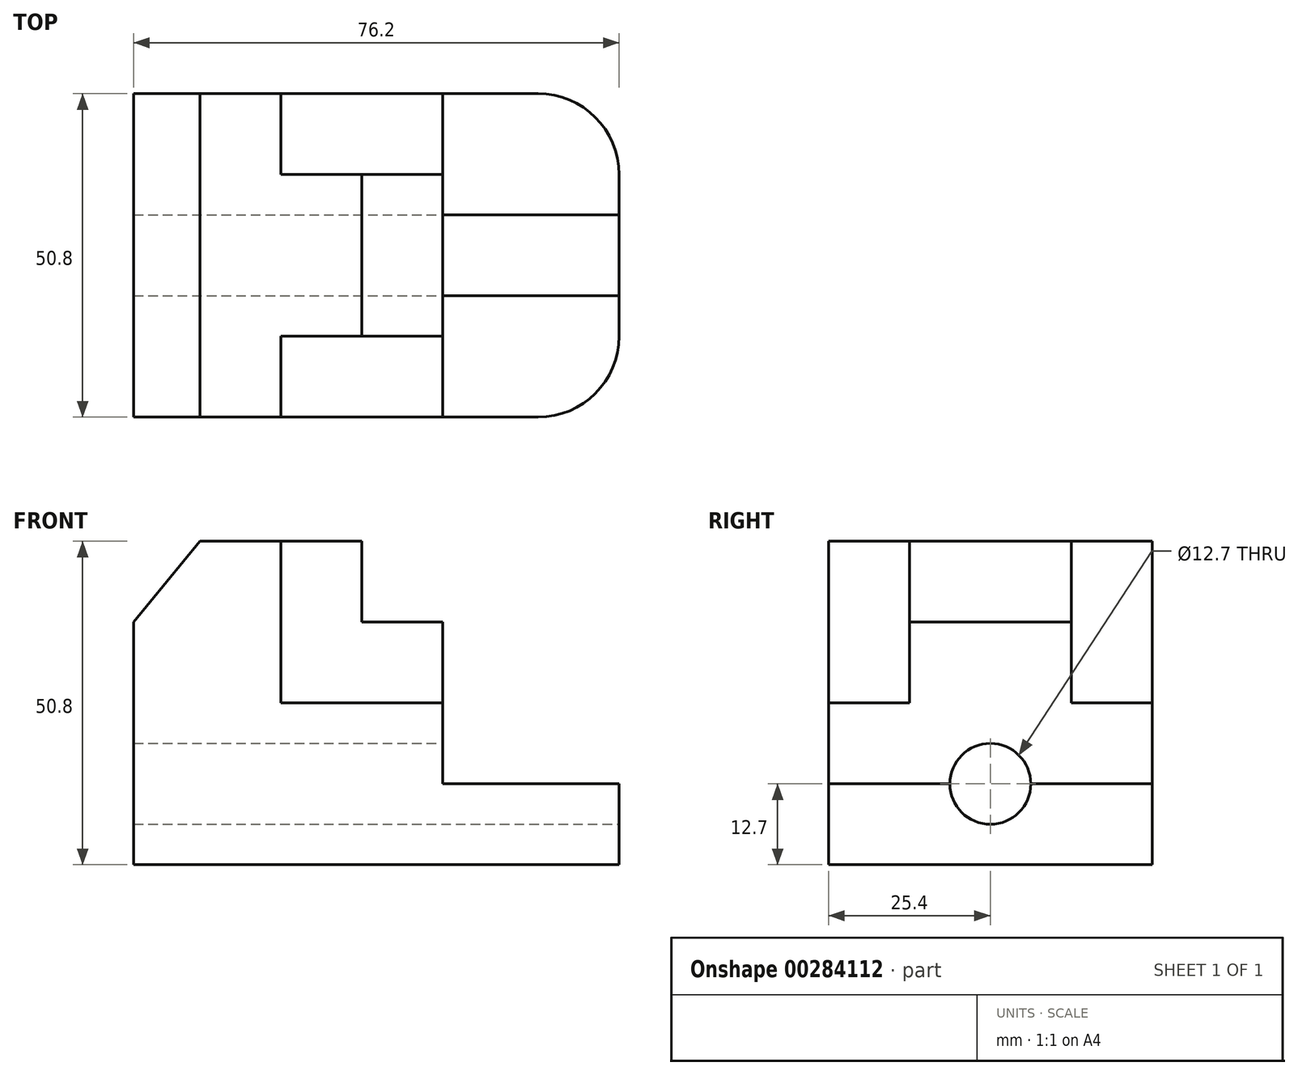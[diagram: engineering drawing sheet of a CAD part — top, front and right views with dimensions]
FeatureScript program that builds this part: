
annotation { "Feature Type Name" : "Feature", "Feature Type Description" : "" }
export const myFeature = defineFeature(function(context is Context, id is Id, definition is map)
    precondition{}
    {
        {
            var Q0;
            Q0=qCreatedBy(makeId("Front.planeOp"),FACE);
            var sketch = newSketch(context, id + "F0", { "sketchPlane" : qUnion([Q0])});
            skLineSegment(sketch, "E0", {"start": v(0, 0) * mm, "end": v(0, 38.1) * mm});
            skLineSegment(sketch, "E1", {"start": v(0, 38.1) * mm, "end": v(10.4, 50.8) * mm});
            skLineSegment(sketch, "E2", {"start": v(10.4, 50.8) * mm, "end": v(35.8, 50.8) * mm});
            skLineSegment(sketch, "E3", {"start": v(35.8, 50.8) * mm, "end": v(35.8, 38.1) * mm});
            skLineSegment(sketch, "E4", {"start": v(35.8, 38.1) * mm, "end": v(48.5, 38.1) * mm});
            skLineSegment(sketch, "E5", {"start": v(48.5, 38.1) * mm, "end": v(48.5, 12.7) * mm});
            skLineSegment(sketch, "E6", {"start": v(48.5, 12.7) * mm, "end": v(76.2, 12.7) * mm});
            skLineSegment(sketch, "E7", {"start": v(76.2, 12.7) * mm, "end": v(76.2, 0) * mm});
            skLineSegment(sketch, "E8", {"start": v(76.2, 0) * mm, "end": v(0, 0) * mm});
            skSolve(sketch);
        }
        {
            var Q0;
            Q0=makeQuery(id+"F0.imprint","IMPRINT",FACE,{"disambiguationData":[TD([[makeQuery(id+"F0.imprint","IMPRINT",EDGE,{"derivedFrom":sQuery(id+"F0.wireOp",EDGE,"E0")}),-1.0]])]});
            extrude(context, id + "F1", {"entities" : qUnion([Q0]), "depth" : 50.8 * mm});
        }
        {
            var Q0;
            Q0=makeQuery(id+"F1.opExtrude","CAP_FACE",FACE,{"disambiguationData":[OSD([sQuery(id+"F0.wireOp",EDGE,"E0"),sQuery(id+"F0.wireOp",EDGE,"E1"),sQuery(id+"F0.wireOp",EDGE,"E2"),sQuery(id+"F0.wireOp",EDGE,"E3"),sQuery(id+"F0.wireOp",EDGE,"E4"),sQuery(id+"F0.wireOp",EDGE,"E5"),sQuery(id+"F0.wireOp",EDGE,"E6"),sQuery(id+"F0.wireOp",EDGE,"E7"),sQuery(id+"F0.wireOp",EDGE,"E8")])],"isStart":false});
            var sketch = newSketch(context, id + "F2", { "sketchPlane" : qUnion([Q0])});
            skLineSegment(sketch, "E9", {"start": v(23.1, 50.8) * mm, "end": v(23.1, 25.4) * mm});
            skLineSegment(sketch, "E10", {"start": v(23.1, 25.4) * mm, "end": v(48.5, 25.4) * mm});
            skLineSegment(sketch, "E11", {"start": v(48.5, 25.4) * mm, "end": v(48.5, 38.1) * mm});
            skLineSegment(sketch, "E12", {"start": v(48.5, 38.1) * mm, "end": v(35.8, 38.1) * mm});
            skLineSegment(sketch, "E13", {"start": v(35.8, 38.1) * mm, "end": v(35.8, 50.8) * mm});
            skLineSegment(sketch, "E14", {"start": v(35.8, 50.8) * mm, "end": v(23.1, 50.8) * mm});
            skSolve(sketch);
        }
        {
            var Q0;
            Q0 = qSketchRegion(id + "F2", true);
            extrude(context, id + "F3", {"entities" : qUnion([Q0]), "operationType" : NewBodyOperationType.REMOVE, "oppositeDirection" : true, "depth" : 12.7 * mm});
        }
        {
            var Q0;
            Q0=makeQuery(id+"F1.opExtrude","CAP_FACE",FACE,{"disambiguationData":[OSD([sQuery(id+"F0.wireOp",EDGE,"E0"),sQuery(id+"F0.wireOp",EDGE,"E1"),sQuery(id+"F0.wireOp",EDGE,"E2"),sQuery(id+"F0.wireOp",EDGE,"E3"),sQuery(id+"F0.wireOp",EDGE,"E4"),sQuery(id+"F0.wireOp",EDGE,"E5"),sQuery(id+"F0.wireOp",EDGE,"E6"),sQuery(id+"F0.wireOp",EDGE,"E7"),sQuery(id+"F0.wireOp",EDGE,"E8")])],"isStart":true});
            var sketch = newSketch(context, id + "F4", { "sketchPlane" : qUnion([Q0])});
            skLineSegment(sketch, "E15", {"start": v(-23.1, 50.8) * mm, "end": v(-23.1, 25.4) * mm});
            skLineSegment(sketch, "E16", {"start": v(-23.1, 25.4) * mm, "end": v(-48.5, 25.4) * mm});
            skLineSegment(sketch, "E17", {"start": v(-48.5, 25.4) * mm, "end": v(-48.5, 38.1) * mm});
            skLineSegment(sketch, "E18", {"start": v(-48.5, 38.1) * mm, "end": v(-35.8, 38.1) * mm});
            skLineSegment(sketch, "E19", {"start": v(-35.8, 38.1) * mm, "end": v(-35.8, 50.8) * mm});
            skLineSegment(sketch, "E20", {"start": v(-35.8, 50.8) * mm, "end": v(-23.1, 50.8) * mm});
            skSolve(sketch);
        }
        {
            var Q0;
            Q0=makeQuery(id+"F4.imprint","IMPRINT",FACE,{"disambiguationData":[TD([[makeQuery(id+"F4.imprint","IMPRINT",EDGE,{"derivedFrom":sQuery(id+"F4.wireOp",EDGE,"E15")}),-1.0]])]});
            extrude(context, id + "F5", {"entities" : qUnion([Q0]), "operationType" : NewBodyOperationType.REMOVE, "oppositeDirection" : true, "depth" : 12.7 * mm});
        }
        {
            var Q0;
            Q0=makeQuery(id+"F1.opExtrude","SWEPT_FACE",FACE,{"disambiguationData":[OSD([sQuery(id+"F0.wireOp",EDGE,"E7")])]});
            var sketch = newSketch(context, id + "F6", { "sketchPlane" : qUnion([Q0])});
            skCircle(sketch, "E21", {"center": v(-25.4, 12.7) * mm, "radius": 6.35 * mm});
            skSolve(sketch);
        }
        {
            var Q0;
            {var subQ0=sQuery(id+"F6.wireOp",EDGE,"E21");var subQ1=makeQuery(id+"F1.opExtrude","SWEPT_EDGE",EDGE,{"disambiguationData":[OSD([sQuery(id+"F0.wireOp",EDGE,"E6"),sQuery(id+"F0.wireOp",EDGE,"E7")])]});var subQ2=makeQuery(id+"F6.imprint","INTERSECT",VERTEX,{"disambiguationData":[OD(0.0)],"derivedFrom":[subQ1,subQ0]});Q0=makeQuery(id+"F6.imprint","IMPRINT",FACE,{"disambiguationData":[TD([[makeQuery(id+"F6.imprint","IMPRINT",EDGE,{"disambiguationData":[TD([[subQ2,-1.0]])],"derivedFrom":subQ0}),1.0]])]});}
            var Q1;
            {var subQ0=sQuery(id+"F6.wireOp",EDGE,"E21");var subQ1=makeQuery(id+"F1.opExtrude","SWEPT_EDGE",EDGE,{"disambiguationData":[OSD([sQuery(id+"F0.wireOp",EDGE,"E6"),sQuery(id+"F0.wireOp",EDGE,"E7")])]});var subQ2=makeQuery(id+"F6.imprint","INTERSECT",VERTEX,{"disambiguationData":[OD(0.0)],"derivedFrom":[subQ1,subQ0]});Q1=makeQuery(id+"F6.imprint","IMPRINT",FACE,{"disambiguationData":[TD([[makeQuery(id+"F6.imprint","IMPRINT",EDGE,{"disambiguationData":[TD([[subQ2,1.0]])],"derivedFrom":subQ0}),1.0]])]});}
            extrude(context, id + "F7", {"entities" : qUnion([Q0, Q1]), "operationType" : NewBodyOperationType.REMOVE, "endBound" : BoundingType.THROUGH_ALL, "oppositeDirection" : true, "depth" : 25.4 * mm});
        }
        {
            var Q0;
            Q0=makeQuery(id+"F1.opExtrude","CAP_EDGE",EDGE,{"disambiguationData":[OSD([sQuery(id+"F0.wireOp",EDGE,"E7")])],"isStart":false});
            var Q1;
            Q1=makeQuery(id+"F1.opExtrude","CAP_EDGE",EDGE,{"disambiguationData":[OSD([sQuery(id+"F0.wireOp",EDGE,"E7")])],"isStart":true});
            fillet(context, id + "F8", {"entities" : qUnion([Q0, Q1]), "radius" : 12.7 * mm, "tangentPropagation" : true, "allowEdgeOverflow" : false});
        }
    });
